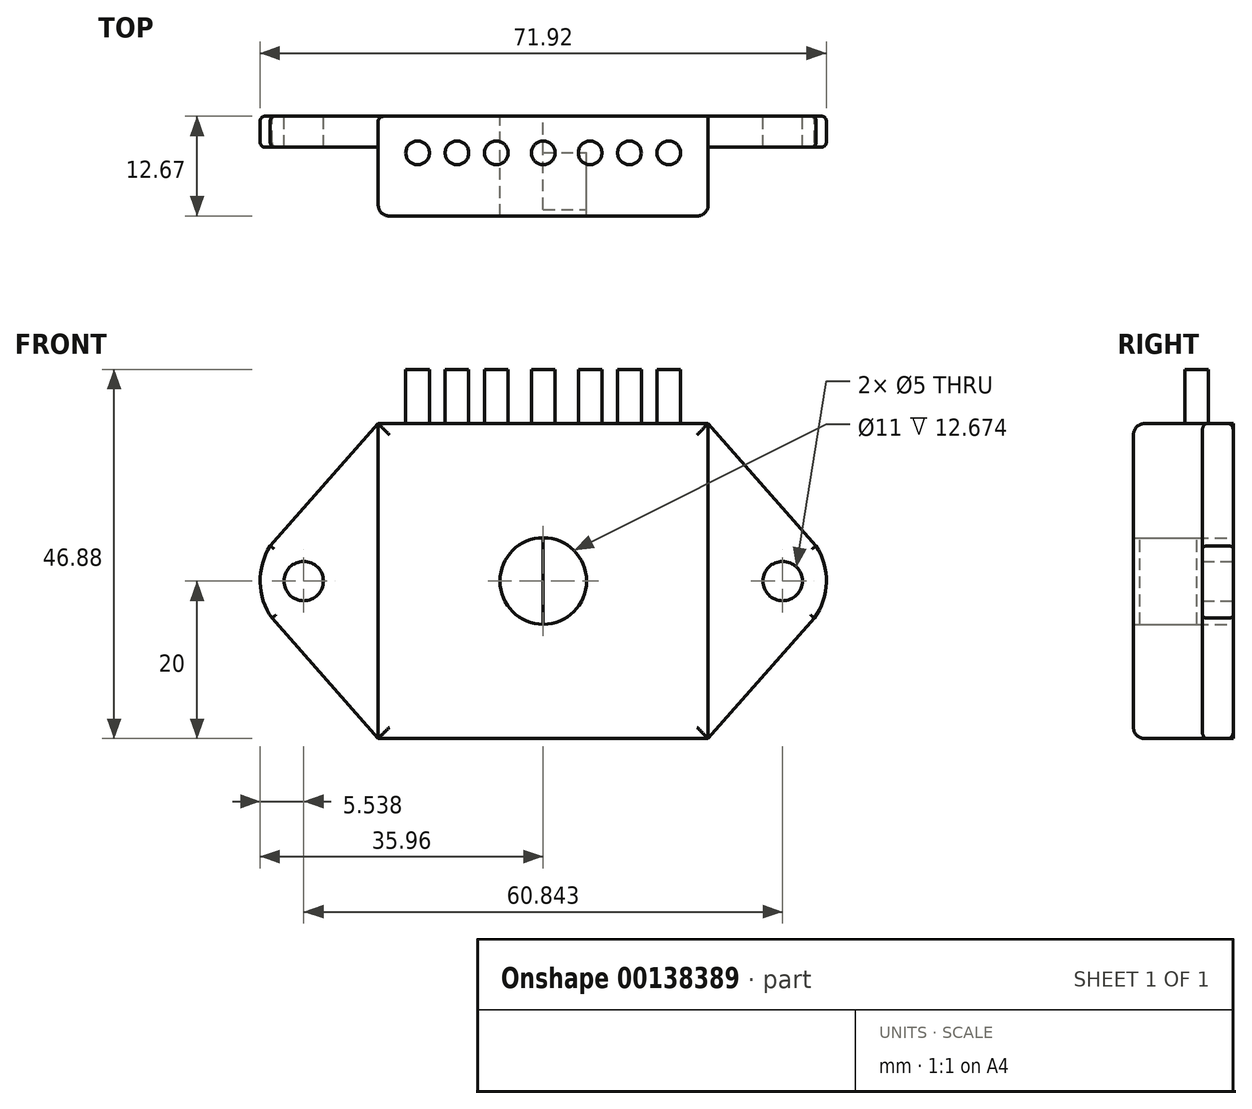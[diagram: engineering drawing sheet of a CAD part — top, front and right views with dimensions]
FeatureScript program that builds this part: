
annotation { "Feature Type Name" : "Feature", "Feature Type Description" : "" }
export const myFeature = defineFeature(function(context is Context, id is Id, definition is map)
    precondition{}
    {
        {
            var Q0;
            Q0=qCreatedBy(makeId("Front.planeOp"),FACE);
            var sketch = newSketch(context, id + "F0", { "sketchPlane" : qUnion([Q0])});
            skLineSegment(sketch, "E0.bottom", {"start": v(0, 0) * mm, "end": v(20.96, 0) * mm});
            skLineSegment(sketch, "E0.top", {"start": v(0, 40) * mm, "end": v(20.96, 40) * mm});
            skLineSegment(sketch, "E0.left", {"start": v(0, 0) * mm, "end": v(0, 40) * mm});
            skLineSegment(sketch, "E0.right", {"start": v(20.96, 0) * mm, "end": v(20.96, 40) * mm});
            skLineSegment(sketch, "E1", {"start": v(20.96, 20) * mm, "end": v(0, 20) * mm, "construction": true});
            skLineSegment(sketch, "E2", {"start": v(0, 20) * mm, "end": v(-39.54, 20) * mm, "construction": true});
            skLineSegment(sketch, "E3", {"start": v(20.96, 20) * mm, "end": v(61.65, 20) * mm, "construction": true});
            skArc(sketch, "E4", {"start": v(0, 14.5) * mm, "mid": v(5.5, 20) * mm, "end": v(0, 25.5) * mm});
            skLineSegment(sketch, "E5", {"start": v(47, 20) * mm, "end": v(20.96, 20) * mm});
            skLineSegment(sketch, "E6", {"start": v(20.96, 40) * mm, "end": v(34.67, 24.46) * mm});
            skLineSegment(sketch, "E7", {"start": v(34.46, 15.3) * mm, "end": v(20.96, 0) * mm});
            skArc(sketch, "E8", {"start": v(34.46, 15.3) * mm, "mid": v(35.96, 19.85) * mm, "end": v(34.67, 24.46) * mm});
            skCircle(sketch, "E9", {"center": v(30.42, 20) * mm, "radius": 2.5 * mm});
            skLineSegment(sketch, "E10.MirrorCS", {"start": v(0, 40) * mm, "end": v(-20.96, 40) * mm});
            skArc(sketch, "E11.MirrorCS", {"start": v(0, 14.5) * mm, "mid": v(-5.5, 20) * mm, "end": v(0, 25.5) * mm});
            skLineSegment(sketch, "E12.MirrorCS", {"start": v(0, 0) * mm, "end": v(-20.96, 0) * mm});
            skLineSegment(sketch, "E13.MirrorCS", {"start": v(-20.96, 0) * mm, "end": v(-20.96, 40) * mm});
            skCircle(sketch, "E14.MirrorC", {"center": v(-30.42, 20) * mm, "radius": 2.5 * mm});
            skLineSegment(sketch, "E15.MirrorCS", {"start": v(-20.96, 40) * mm, "end": v(-34.67, 24.46) * mm});
            skArc(sketch, "E16.MirrorCS", {"start": v(-34.46, 15.3) * mm, "mid": v(-35.96, 19.85) * mm, "end": v(-34.67, 24.46) * mm});
            skLineSegment(sketch, "E17.MirrorCS", {"start": v(-34.46, 15.3) * mm, "end": v(-20.96, 0) * mm});
            skSolve(sketch);
        }
        {
            var Q0;
            {var subQ0=sQuery(id+"F0.wireOp",EDGE,"E10.MirrorCS");Q0=makeQuery(id+"F0.imprint","IMPRINT",FACE,{"disambiguationData":[TD([[makeQuery(id+"F0.imprint","IMPRINT",EDGE,{"derivedFrom":subQ0}),1.0]])]});}
            var Q1;
            {var subQ4=sQuery(id+"F0.wireOp",EDGE,"E0.bottom");Q1=makeQuery(id+"F0.imprint","IMPRINT",FACE,{"disambiguationData":[TD([[makeQuery(id+"F0.imprint","IMPRINT",EDGE,{"derivedFrom":subQ4}),1.0]])]});}
            extrude(context, id + "F1", {"entities" : qUnion([Q0, Q1]), "depth" : 12.67 * mm});
        }
        {
            var Q0;
            {var subQ0=sQuery(id+"F0.wireOp",EDGE,"E7");Q0=makeQuery(id+"F0.imprint","IMPRINT",FACE,{"disambiguationData":[TD([[makeQuery(id+"F0.imprint","IMPRINT",EDGE,{"derivedFrom":subQ0}),-1.0]])]});}
            var Q1;
            Q1=makeQuery(id+"F0.imprint","IMPRINT",FACE,{"disambiguationData":[TD([[makeQuery(id+"F0.imprint","IMPRINT",EDGE,{"derivedFrom":sQuery(id+"F0.wireOp",EDGE,"E13.MirrorCS")}),1.0]])]});
            var Q2;
            {var subQ0=sQuery(id+"F0.wireOp",EDGE,"E6");Q2=makeQuery(id+"F0.imprint","IMPRINT",FACE,{"disambiguationData":[TD([[makeQuery(id+"F0.imprint","IMPRINT",EDGE,{"derivedFrom":subQ0}),-1.0]])]});}
            extrude(context, id + "F2", {"entities" : qUnion([Q0, Q1, Q2]), "depth" : 3.92 * mm});
        }
        {
            var Q0;
            {var subQ1=sQuery(id+"F0.wireOp",EDGE,"E4");Q0=makeQuery(id+"F0.imprint","IMPRINT",FACE,{"disambiguationData":[TD([[makeQuery(id+"F0.imprint","IMPRINT",EDGE,{"derivedFrom":subQ1}),1.0]])]});}
            var Q1;
            {var subQ0=sQuery(id+"F0.wireOp",EDGE,"E11.MirrorCS");Q1=makeQuery(id+"F0.imprint","IMPRINT",FACE,{"disambiguationData":[TD([[makeQuery(id+"F0.imprint","IMPRINT",EDGE,{"derivedFrom":subQ0}),-1.0]])]});}
            extrude(context, id + "F3", {"entities" : qUnion([Q0, Q1]), "operationType" : NewBodyOperationType.ADD, "depth" : 4.63 * mm});
        }
        {
            var Q0;
            Q0=makeQuery(id+"F1.opExtrude","CAP_EDGE",EDGE,{"disambiguationData":[OSD([sQuery(id+"F0.wireOp",EDGE,"E0.bottom"),sQuery(id+"F0.wireOp",EDGE,"E12.MirrorCS")])],"isStart":false});
            var Q1;
            Q1=makeQuery(id+"F1.opExtrude","CAP_EDGE",EDGE,{"disambiguationData":[OSD([sQuery(id+"F0.wireOp",EDGE,"E0.right")])],"isStart":false});
            var Q2;
            Q2=makeQuery(id+"F1.opExtrude","CAP_EDGE",EDGE,{"disambiguationData":[OSD([sQuery(id+"F0.wireOp",EDGE,"E13.MirrorCS")])],"isStart":false});
            var Q3;
            Q3=makeQuery(id+"F1.opExtrude","CAP_EDGE",EDGE,{"disambiguationData":[OSD([sQuery(id+"F0.wireOp",EDGE,"E0.top"),sQuery(id+"F0.wireOp",EDGE,"E10.MirrorCS")])],"isStart":false});
            fillet(context, id + "F4", {"entities" : qUnion([Q0, Q1, Q2, Q3]), "radius" : 1.42 * mm, "tangentPropagation" : true, "allowEdgeOverflow" : false});
        }
        {
            var Q0;
            Q0=makeQuery(id+"F3.opExtrude","CAP_FACE",FACE,{"disambiguationData":[OSD([sQuery(id+"F0.wireOp",EDGE,"E4"),sQuery(id+"F0.wireOp",EDGE,"E11.MirrorCS")])],"isStart":false});
            extrude(context, id + "F5", {"entities" : qUnion([Q0]), "depth" : 7.2 * mm});
        }
        {
            var Q0;
            Q0=makeQuery(id+"F2.opExtrude","CAP_EDGE",EDGE,{"disambiguationData":[OSD([sQuery(id+"F0.wireOp",EDGE,"E7")])],"isStart":false});
            var Q1;
            Q1=makeQuery(id+"F2.opExtrude","CAP_EDGE",EDGE,{"disambiguationData":[OSD([sQuery(id+"F0.wireOp",EDGE,"E8")])],"isStart":false});
            var Q2;
            Q2=makeQuery(id+"F2.opExtrude","CAP_EDGE",EDGE,{"disambiguationData":[OSD([sQuery(id+"F0.wireOp",EDGE,"E6")])],"isStart":false});
            var Q3;
            Q3=makeQuery(id+"F2.opExtrude","CAP_EDGE",EDGE,{"disambiguationData":[OSD([sQuery(id+"F0.wireOp",EDGE,"E7")])],"isStart":true});
            var Q4;
            Q4=makeQuery(id+"F2.opExtrude","CAP_EDGE",EDGE,{"disambiguationData":[OSD([sQuery(id+"F0.wireOp",EDGE,"E8")])],"isStart":true});
            var Q5;
            Q5=makeQuery(id+"F2.opExtrude","CAP_EDGE",EDGE,{"disambiguationData":[OSD([sQuery(id+"F0.wireOp",EDGE,"E6")])],"isStart":true});
            var Q6;
            Q6=makeQuery(id+"F2.opExtrude","CAP_EDGE",EDGE,{"disambiguationData":[OSD([sQuery(id+"F0.wireOp",EDGE,"E15.MirrorCS")])],"isStart":false});
            var Q7;
            Q7=makeQuery(id+"F2.opExtrude","CAP_EDGE",EDGE,{"disambiguationData":[OSD([sQuery(id+"F0.wireOp",EDGE,"E16.MirrorCS")])],"isStart":false});
            var Q8;
            Q8=makeQuery(id+"F2.opExtrude","CAP_EDGE",EDGE,{"disambiguationData":[OSD([sQuery(id+"F0.wireOp",EDGE,"E17.MirrorCS")])],"isStart":false});
            var Q9;
            Q9=makeQuery(id+"F2.opExtrude","CAP_EDGE",EDGE,{"disambiguationData":[OSD([sQuery(id+"F0.wireOp",EDGE,"E15.MirrorCS")])],"isStart":true});
            var Q10;
            Q10=makeQuery(id+"F2.opExtrude","CAP_EDGE",EDGE,{"disambiguationData":[OSD([sQuery(id+"F0.wireOp",EDGE,"E16.MirrorCS")])],"isStart":true});
            var Q11;
            Q11=makeQuery(id+"F2.opExtrude","CAP_EDGE",EDGE,{"disambiguationData":[OSD([sQuery(id+"F0.wireOp",EDGE,"E17.MirrorCS")])],"isStart":true});
            fillet(context, id + "F6", {"entities" : qUnion([Q0, Q1, Q2, Q3, Q4, Q5, Q6, Q7, Q8, Q9, Q10, Q11]), "radius" : .6 * mm, "tangentPropagation" : true, "allowEdgeOverflow" : false});
        }
        {
            var Q0;
            Q0=makeQuery(id+"F1.opExtrude","SWEPT_FACE",FACE,{"disambiguationData":[OSD([sQuery(id+"F0.wireOp",EDGE,"E0.top"),sQuery(id+"F0.wireOp",EDGE,"E10.MirrorCS")])]});
            var sketch = newSketch(context, id + "F7", { "sketchPlane" : qUnion([Q0])});
            skLineSegment(sketch, "E18", {"start": v(20.96, -4.65) * mm, "end": v(-20.96, -4.65) * mm, "construction": true});
            skCircle(sketch, "E19", {"center": v(15.96, -4.65) * mm, "radius": 1.5 * mm});
            skCircle(sketch, "E20", {"center": v(10.96, -4.65) * mm, "radius": 1.5 * mm});
            skArc(sketch, "E21", {"start": v(0, -6.15) * mm, "mid": v(1.5, -4.65) * mm, "end": v(0, -3.15) * mm});
            skCircle(sketch, "E22", {"center": v(5.96, -4.65) * mm, "radius": 1.5 * mm});
            skLineSegment(sketch, "E23", {"start": v(0, 0) * mm, "end": v(0, -11.26) * mm, "construction": true});
            skArc(sketch, "E24.MirrorCS", {"start": v(0, -6.15) * mm, "mid": v(-1.5, -4.65) * mm, "end": v(0, -3.15) * mm});
            skCircle(sketch, "E25.MirrorC", {"center": v(-5.96, -4.65) * mm, "radius": 1.5 * mm});
            skCircle(sketch, "E26.MirrorC", {"center": v(-10.96, -4.65) * mm, "radius": 1.5 * mm});
            skCircle(sketch, "E27.MirrorC", {"center": v(-15.96, -4.65) * mm, "radius": 1.5 * mm});
            skSolve(sketch);
        }
        {
            var Q0;
            Q0 = qSketchRegion(id + "F7", true);
            extrude(context, id + "F8", {"entities" : qUnion([Q0]), "depth" : 6.88 * mm});
        }
    });
